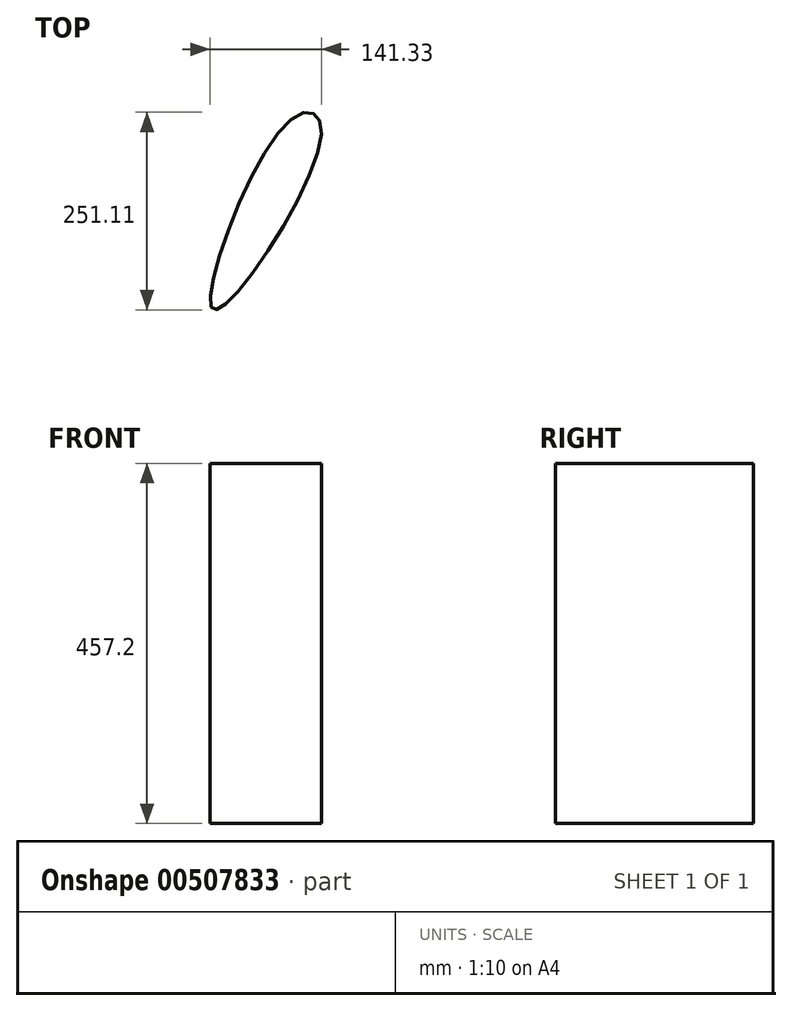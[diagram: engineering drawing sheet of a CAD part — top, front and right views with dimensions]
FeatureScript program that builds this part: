
annotation { "Feature Type Name" : "Feature", "Feature Type Description" : "" }
export const myFeature = defineFeature(function(context is Context, id is Id, definition is map)
    precondition{}
    {
        {
            var Q0;
            Q0=qCreatedBy(makeId("Top.planeOp"),FACE);
            var sketch = newSketch(context, id + "F0", { "sketchPlane" : qUnion([Q0])});
            skFitSpline(sketch, "E0", {"points": [v(0, 117.25) * mm, v(-98.72, -124.46) * mm, v(38.38, 102.48) * mm, v(0, 117.25) * mm]});
            skLineSegment(sketch, "E1", {"start": v(-98.72, -124.46) * mm, "end": v(30.18, 123.43) * mm, "construction": true});
            skSolve(sketch);
        }
        {
            var Q0;
            Q0=makeQuery(id+"F0.imprint","IMPRINT",FACE,{"disambiguationData":[TD([[makeQuery(id+"F0.imprint","IMPRINT",EDGE,{"derivedFrom":sQuery(id+"F0.wireOp",EDGE,"E0")}),1.0]])]});
            extrude(context, id + "F1", {"entities" : qUnion([Q0]), "depth" : 457.2 * mm, "offsetDistance" : 25.4 * mm});
        }
    });
